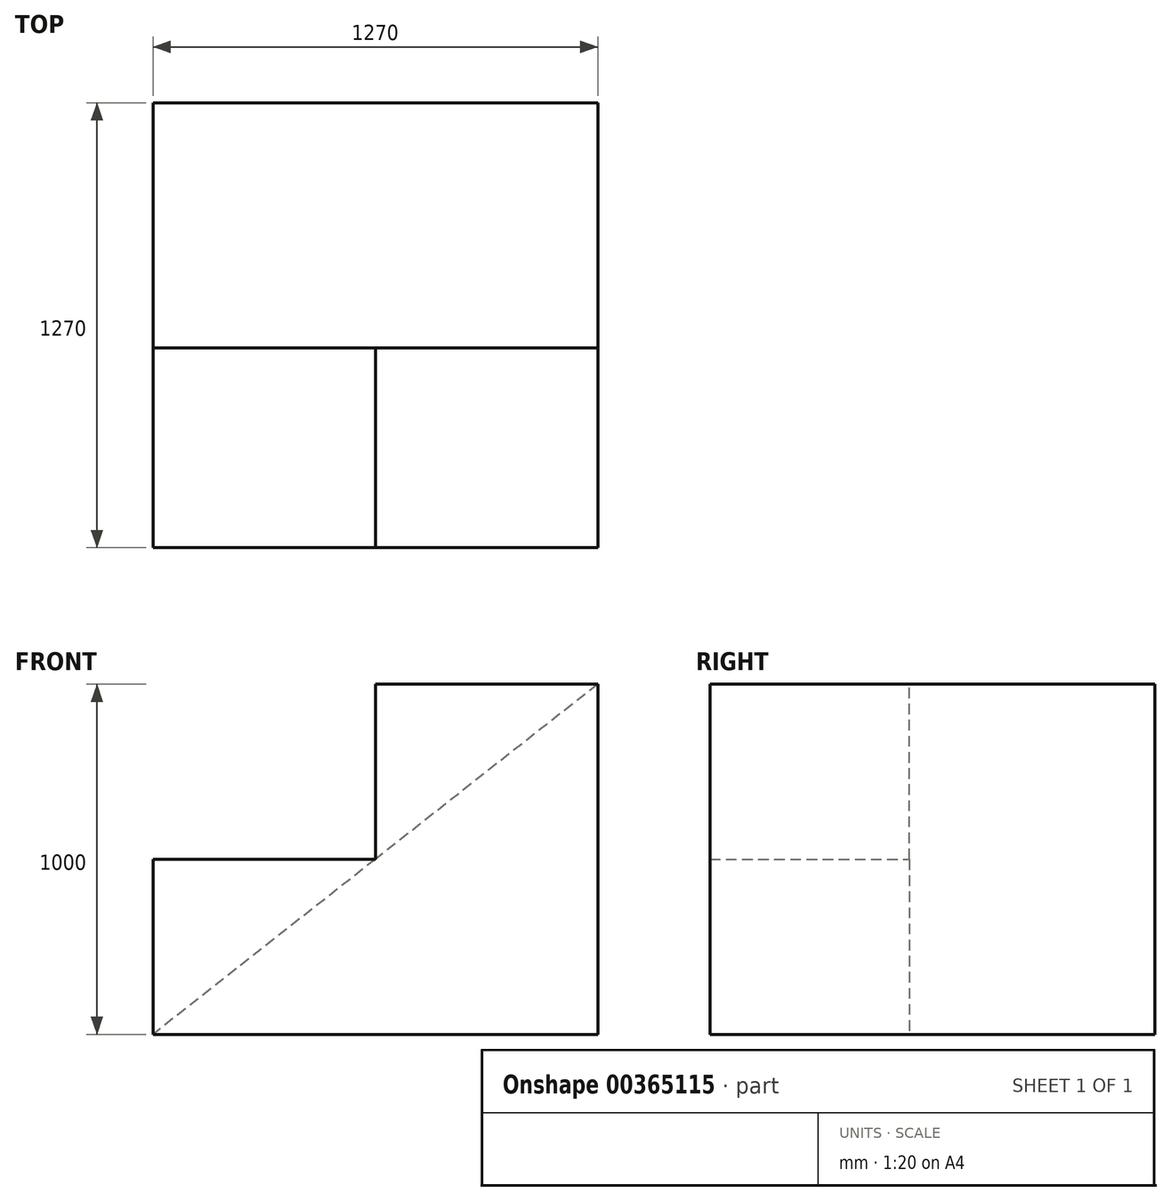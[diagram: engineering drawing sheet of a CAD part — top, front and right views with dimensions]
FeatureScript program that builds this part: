
annotation { "Feature Type Name" : "Feature", "Feature Type Description" : "" }
export const myFeature = defineFeature(function(context is Context, id is Id, definition is map)
    precondition{}
    {
        {
            var Q0;
            Q0=qCreatedBy(makeId("Top.planeOp"),FACE);
            var sketch = newSketch(context, id + "F0", { "sketchPlane" : qUnion([Q0])});
            skLineSegment(sketch, "E0.bottom", {"start": v(0, 0) * mm, "end": v(1270, 0) * mm});
            skLineSegment(sketch, "E0.top", {"start": v(0, 1270) * mm, "end": v(1270, 1270) * mm});
            skLineSegment(sketch, "E0.left", {"start": v(0, 0) * mm, "end": v(0, 1270) * mm});
            skLineSegment(sketch, "E0.right", {"start": v(1270, 0) * mm, "end": v(1270, 1270) * mm});
            skSolve(sketch);
        }
        {
            var Q0;
            Q0 = qSketchRegion(id + "F0", true);
            extrude(context, id + "F1", {"entities" : qUnion([Q0]), "depth" : 1000 * mm});
        }
        {
            var Q0;
            Q0=makeQuery(id+"F1.opExtrude","CAP_FACE",FACE,{"disambiguationData":[OSD([sQuery(id+"F0.wireOp",EDGE,"E0.bottom"),sQuery(id+"F0.wireOp",EDGE,"E0.top"),sQuery(id+"F0.wireOp",EDGE,"E0.left"),sQuery(id+"F0.wireOp",EDGE,"E0.right")])],"isStart":false});
            var sketch = newSketch(context, id + "F2", { "sketchPlane" : qUnion([Q0])});
            skPoint(sketch, "E1.oppositeSnap0", {"position": v(635, 0) * mm});
            skLineSegment(sketch, "E1.bottom", {"start": v(0, 0) * mm, "end": v(635, 0) * mm});
            skLineSegment(sketch, "E1.top", {"start": v(0, 626.06) * mm, "end": v(635, 626.06) * mm});
            skLineSegment(sketch, "E1.left", {"start": v(0, 0) * mm, "end": v(0, 626.06) * mm});
            skLineSegment(sketch, "E1.right", {"start": v(635, 0) * mm, "end": v(635, 626.06) * mm});
            skSolve(sketch);
        }
        {
            var Q0;
            Q0=makeQuery(id+"F2.imprint","IMPRINT",FACE,{"disambiguationData":[TD([[makeQuery(id+"F2.imprint","IMPRINT",EDGE,{"derivedFrom":sQuery(id+"F2.wireOp",EDGE,"E1.bottom")}),1.0]])]});
            extrude(context, id + "F3", {"entities" : qUnion([Q0]), "operationType" : NewBodyOperationType.REMOVE, "oppositeDirection" : true, "depth" : 500 * mm});
        }
        {
            var Q0;
            Q0=makeQuery(id+"F1.opExtrude","SWEPT_FACE",FACE,{"disambiguationData":[OSD([sQuery(id+"F0.wireOp",EDGE,"E0.top")])]});
            var sketch = newSketch(context, id + "F4", { "sketchPlane" : qUnion([Q0])});
            skLineSegment(sketch, "E2", {"start": v(-1270, 1000) * mm, "end": v(0, 0) * mm});
            skLineSegment(sketch, "E3", {"start": v(0, 0) * mm, "end": v(0, 1000) * mm});
            skLineSegment(sketch, "E4", {"start": v(0, 1000) * mm, "end": v(-1270, 1000) * mm});
            skSolve(sketch);
        }
        {
            var Q0;
            Q0 = qSketchRegion(id + "F4", true);
            extrude(context, id + "F5", {"entities" : qUnion([Q0]), "operationType" : NewBodyOperationType.REMOVE, "oppositeDirection" : true, "depth" : 700 * mm});
        }
    });
